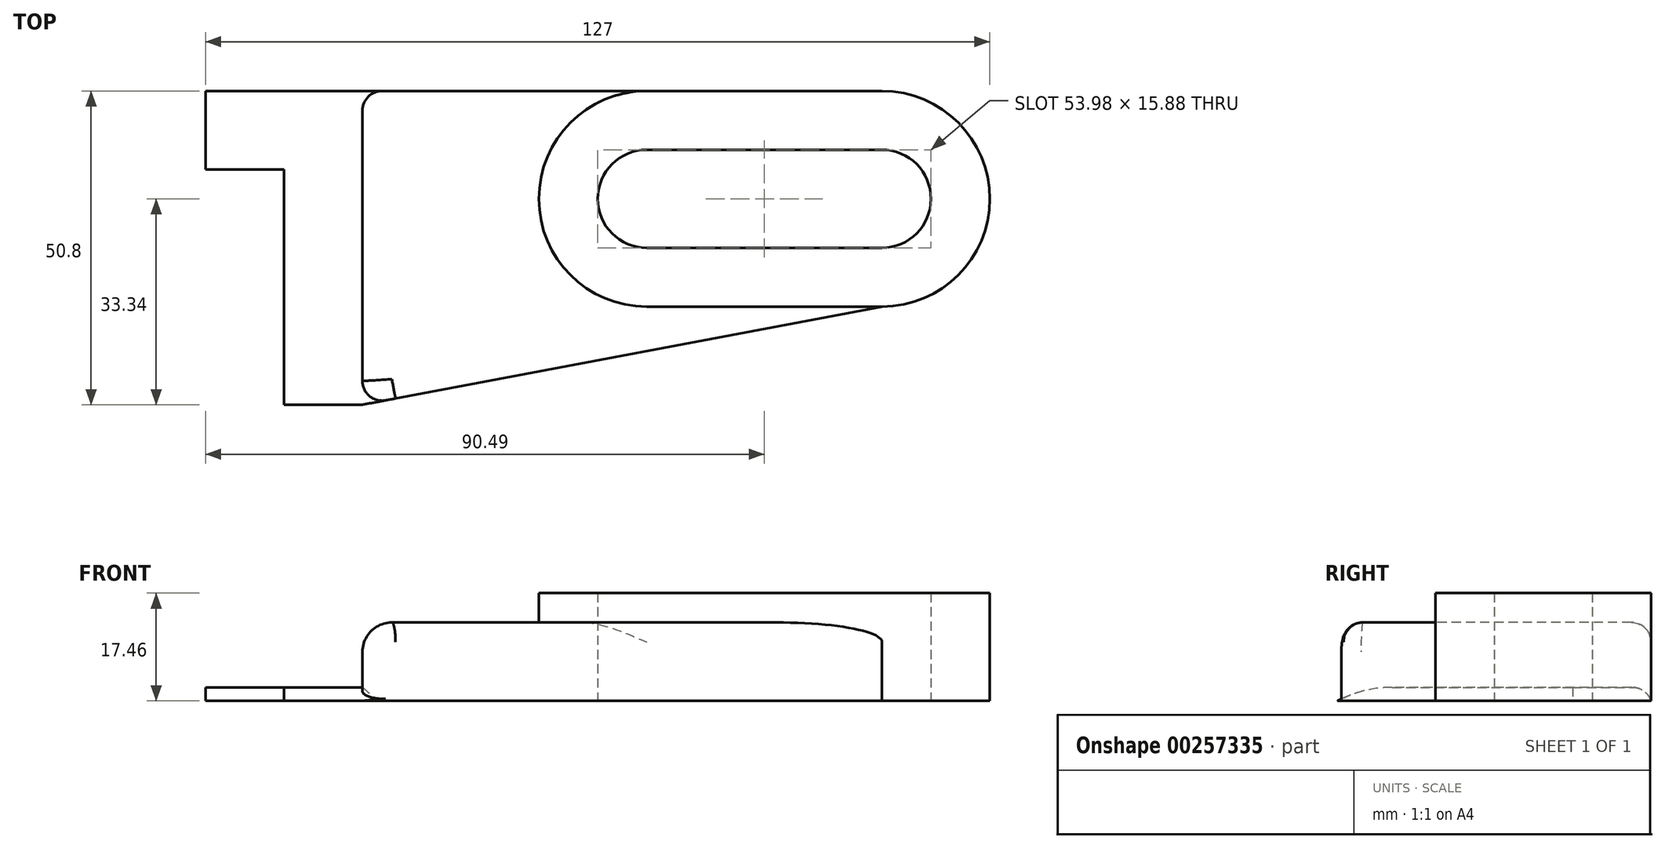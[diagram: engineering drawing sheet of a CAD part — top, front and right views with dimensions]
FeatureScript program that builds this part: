
annotation { "Feature Type Name" : "Feature", "Feature Type Description" : "" }
export const myFeature = defineFeature(function(context is Context, id is Id, definition is map)
    precondition{}
    {
        {
            var Q0;
            Q0=qCreatedBy(makeId("Top.planeOp"),FACE);
            var sketch = newSketch(context, id + "F0", { "sketchPlane" : qUnion([Q0])});
            skArc(sketch, "E0", {"start": v(0, -17.46) * mm, "mid": v(17.46, 0) * mm, "end": v(0, 17.46) * mm});
            skArc(sketch, "E1", {"start": v(-38.1, 17.46) * mm, "mid": v(-55.56, 0) * mm, "end": v(-38.1, -17.46) * mm});
            skArc(sketch, "E2", {"start": v(-38.1, 7.94) * mm, "mid": v(-46.04, 0) * mm, "end": v(-38.1, -7.94) * mm});
            skArc(sketch, "E3", {"start": v(0, -7.94) * mm, "mid": v(7.94, 0) * mm, "end": v(0, 7.94) * mm});
            skLineSegment(sketch, "E4", {"start": v(0, -17.46) * mm, "end": v(0, 17.46) * mm, "construction": true});
            skLineSegment(sketch, "E5", {"start": v(0, 17.46) * mm, "end": v(-84.14, 17.46) * mm});
            skLineSegment(sketch, "E6", {"start": v(-38.1, -17.46) * mm, "end": v(0, -17.46) * mm});
            skLineSegment(sketch, "E7", {"start": v(-38.1, 7.94) * mm, "end": v(0, 7.94) * mm});
            skLineSegment(sketch, "E8", {"start": v(-38.1, -7.94) * mm, "end": v(0, -7.94) * mm});
            skLineSegment(sketch, "E9", {"start": v(-84.14, 17.46) * mm, "end": v(-84.14, -33.34) * mm});
            skLineSegment(sketch, "E10", {"start": v(-84.14, -33.34) * mm, "end": v(0, -17.46) * mm});
            skLineSegment(sketch, "E11", {"start": v(-84.14, -33.34) * mm, "end": v(-96.84, -33.34) * mm});
            skLineSegment(sketch, "E12", {"start": v(-96.84, -33.34) * mm, "end": v(-96.84, 4.76) * mm});
            skLineSegment(sketch, "E13", {"start": v(-96.84, 4.76) * mm, "end": v(-109.54, 4.76) * mm});
            skLineSegment(sketch, "E14", {"start": v(-109.54, 4.76) * mm, "end": v(-109.54, 17.46) * mm});
            skLineSegment(sketch, "E15", {"start": v(-109.54, 17.46) * mm, "end": v(-84.14, 17.46) * mm});
            skLineSegment(sketch, "E16", {"start": v(-96.84, 4.76) * mm, "end": v(-96.84, 17.46) * mm, "construction": true});
            skLineSegment(sketch, "E17", {"start": v(-38.1, -17.46) * mm, "end": v(-38.1, 17.46) * mm, "construction": true});
            skSolve(sketch);
        }
        {
            var Q0;
            {var subQ2=sQuery(id+"F0.wireOp",EDGE,"E1");Q0=makeQuery(id+"F0.imprint","IMPRINT",FACE,{"disambiguationData":[TD([[makeQuery(id+"F0.imprint","IMPRINT",EDGE,{"derivedFrom":subQ2}),-1.0]])]});}
            extrude(context, id + "F1", {"entities" : qUnion([Q0]), "depth" : 12.7 * mm});
        }
        {
            var Q0;
            {var subQ1=sQuery(id+"F0.wireOp",EDGE,"E0");Q0=makeQuery(id+"F0.imprint","IMPRINT",FACE,{"disambiguationData":[TD([[makeQuery(id+"F0.imprint","IMPRINT",EDGE,{"derivedFrom":subQ1}),1.0]])]});}
            extrude(context, id + "F2", {"entities" : qUnion([Q0]), "operationType" : NewBodyOperationType.ADD, "depth" : 17.46 * mm});
        }
        {
            var Q0;
            Q0=makeQuery(id+"F0.imprint","IMPRINT",FACE,{"disambiguationData":[TD([[makeQuery(id+"F0.imprint","IMPRINT",EDGE,{"derivedFrom":sQuery(id+"F0.wireOp",EDGE,"E9")}),-1.0]])]});
            extrude(context, id + "F3", {"entities" : qUnion([Q0]), "operationType" : NewBodyOperationType.ADD, "depth" : (2 + (3 / 16)) * mm});
        }
        {
            var Q0;
            Q0=makeQuery(id+"F1.opExtrude","CAP_EDGE",EDGE,{"disambiguationData":[OSD([sQuery(id+"F0.wireOp",EDGE,"E9")])],"isStart":false});
            var Q1;
            Q1=makeQuery(id+"F1.opExtrude","CAP_EDGE",EDGE,{"disambiguationData":[OSD([sQuery(id+"F0.wireOp",EDGE,"E1")])],"isStart":false});
            var Q2;
            Q2=makeQuery(id+"F1.opExtrude","CAP_EDGE",EDGE,{"disambiguationData":[OSD([sQuery(id+"F0.wireOp",EDGE,"E6")])],"isStart":false});
            fillet(context, id + "F4", {"entities" : qUnion([Q0, Q1, Q2]), "radius" : 4.76 * mm, "tangentPropagation" : true, "allowEdgeOverflow" : false});
        }
        {
            var Q0;
            Q0=makeQuery(id+"F3.opExtrude","CAP_EDGE",EDGE,{"disambiguationData":[OSD([sQuery(id+"F0.wireOp",EDGE,"E11")])],"isStart":false});
            fillet(context, id + "F5", {"entities" : qUnion([Q0]), "radius" : 19.05 * mm, "tangentPropagation" : true, "allowEdgeOverflow" : false});
        }
        {
            var Q0;
            Q0=makeQuery(id+"F1.opExtrude","CAP_EDGE",EDGE,{"disambiguationData":[OSD([sQuery(id+"F0.wireOp",EDGE,"E10")])],"isStart":false});
            var Q1;
            Q1=makeQuery(id+"F4.opFillet","BLEND_EDGE",EDGE,{"blendedFrom":[makeQuery(id+"F1.opExtrude","CAP_EDGE",EDGE,{"disambiguationData":[OSD([sQuery(id+"F0.wireOp",EDGE,"E9")])],"isStart":false}),makeQuery(id+"F1.opExtrude","SWEPT_FACE",FACE,{"disambiguationData":[OSD([sQuery(id+"F0.wireOp",EDGE,"E10")])]})],"blendedInto":[makeQuery(id+"F1.opExtrude","SWEPT_FACE",FACE,{"disambiguationData":[OSD([sQuery(id+"F0.wireOp",EDGE,"E10")])]})]});
            var Q2;
            Q2=makeQuery(id+"F3.boolean.opBoolean","SPLIT",EDGE,{"derivedFrom":makeQuery(id+"F3.opExtrude","SWEPT_EDGE",EDGE,{"disambiguationData":[OSD([sQuery(id+"F0.wireOp",EDGE,"E9"),sQuery(id+"F0.wireOp",EDGE,"E10"),sQuery(id+"F0.wireOp",EDGE,"E11")])]})});
            var Q3;
            Q3=makeQuery(id+"F5.opFillet","BLEND_EDGE",EDGE,{"blendedFrom":[makeQuery(id+"F3.opExtrude","CAP_EDGE",EDGE,{"disambiguationData":[OSD([sQuery(id+"F0.wireOp",EDGE,"E11")])],"isStart":false}),makeQuery(id+"F3.opExtrude","SWEPT_FACE",FACE,{"disambiguationData":[OSD([sQuery(id+"F0.wireOp",EDGE,"E9")])]})],"blendedInto":[makeQuery(id+"F3.opExtrude","SWEPT_FACE",FACE,{"disambiguationData":[OSD([sQuery(id+"F0.wireOp",EDGE,"E9")])]})]});
            var Q4;
            Q4=makeQuery(id+"F3.opExtrude","CAP_EDGE",EDGE,{"disambiguationData":[OSD([sQuery(id+"F0.wireOp",EDGE,"E9")])],"isStart":false});
            var Q5;
            Q5=makeQuery(id+"F3.opExtrude","CAP_EDGE",EDGE,{"disambiguationData":[OSD([sQuery(id+"F0.wireOp",EDGE,"E15")])],"isStart":false});
            var Q6;
            Q6=makeQuery(id+"F3.opExtrude","SWEPT_EDGE",EDGE,{"disambiguationData":[OSD([sQuery(id+"F0.wireOp",EDGE,"AeLPGbmd-sWzi-xGvD-d3mL-HdhPmddn4cD2"),sQuery(id+"F0.wireOp",EDGE,"E9"),sQuery(id+"F0.wireOp",EDGE,"E15")])]});
            var Q7;
            {var subQ0=sQuery(id+"F0.wireOp",EDGE,"AeLPGbmd-sWzi-xGvD-d3mL-HdhPmddn4cD2");Q7=makeQuery(id+"F4.opFillet","BLEND_EDGE",EDGE,{"blendedFrom":[makeQuery(id+"F1.opExtrude","CAP_EDGE",EDGE,{"disambiguationData":[OSD([sQuery(id+"F0.wireOp",EDGE,"E9")])],"isStart":false}),makeQuery(id+"F3.boolean.opBoolean","MERGE",FACE,{"derivedFrom":[makeQuery(id+"F2.boolean.opBoolean","MERGE",FACE,{"derivedFrom":[makeQuery(id+"F1.opExtrude","SWEPT_FACE",FACE,{"disambiguationData":[OSD([subQ0])]}),makeQuery(id+"F2.opExtrude","SWEPT_FACE",FACE,{"disambiguationData":[OSD([subQ0])]})]}),makeQuery(id+"F3.opExtrude","SWEPT_FACE",FACE,{"disambiguationData":[OSD([sQuery(id+"F0.wireOp",EDGE,"E15")])]})]})],"blendedInto":[makeQuery(id+"F3.boolean.opBoolean","MERGE",FACE,{"derivedFrom":[makeQuery(id+"F2.boolean.opBoolean","MERGE",FACE,{"derivedFrom":[makeQuery(id+"F1.opExtrude","SWEPT_FACE",FACE,{"disambiguationData":[OSD([subQ0])]}),makeQuery(id+"F2.opExtrude","SWEPT_FACE",FACE,{"disambiguationData":[OSD([subQ0])]})]}),makeQuery(id+"F3.opExtrude","SWEPT_FACE",FACE,{"disambiguationData":[OSD([sQuery(id+"F0.wireOp",EDGE,"E15")])]})]})]});}
            var Q8;
            Q8=makeQuery(id+"F1.opExtrude","CAP_EDGE",EDGE,{"disambiguationData":[OSD([sQuery(id+"F0.wireOp",EDGE,"AeLPGbmd-sWzi-xGvD-d3mL-HdhPmddn4cD2")])],"isStart":false});
            fillet(context, id + "F6", {"entities" : qUnion([Q0, Q1, Q2, Q3, Q4, Q5, Q6, Q7, Q8]), "radius" : 3.17 * mm, "tangentPropagation" : true, "allowEdgeOverflow" : false});
        }
        {
            var Q0;
            Q0=qCreatedBy(makeId("Right.planeOp"),FACE);
            var sketch = newSketch(context, id + "F7", { "sketchPlane" : qUnion([Q0])});
            skCircle(sketch, "E18", {"center": v(-14.29, 36.51) * mm, "radius": 7.14 * mm});
            skSolve(sketch);
        }
        {
            var Q0;
            Q0=makeQuery(id+"F7.imprint","IMPRINT",FACE,{"disambiguationData":[TD([[makeQuery(id+"F7.imprint","IMPRINT",EDGE,{"derivedFrom":sQuery(id+"F7.wireOp",EDGE,"E18")}),1.0]])]});
            extrude(context, id + "F8", {"entities" : qUnion([Q0]), "operationType" : NewBodyOperationType.REMOVE, "oppositeDirection" : true, "depth" : 152.4 * mm});
        }
    });
